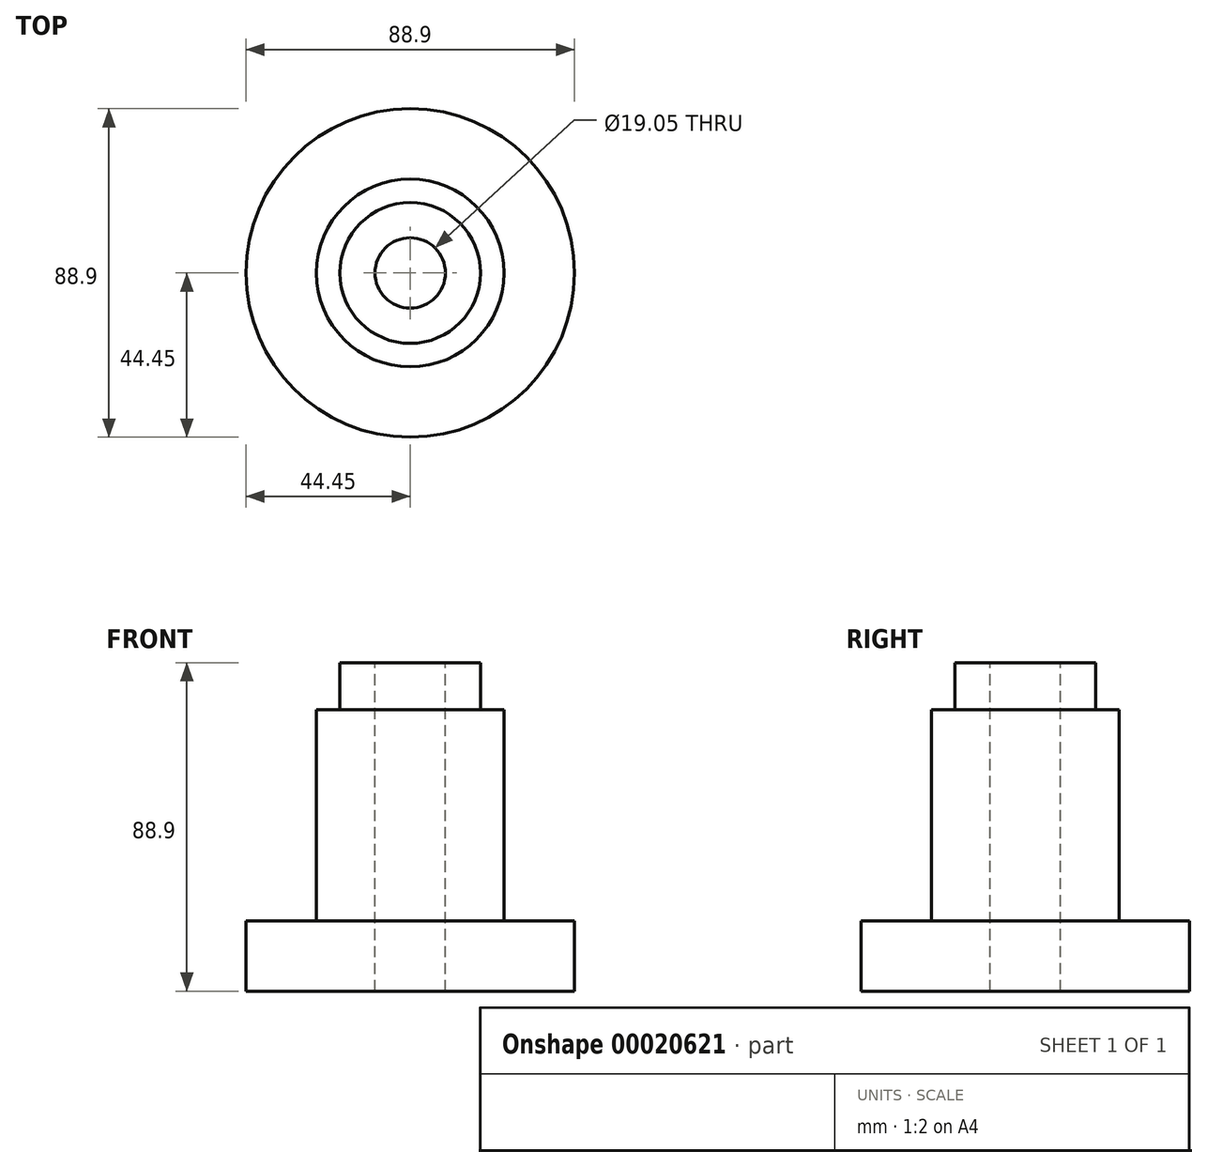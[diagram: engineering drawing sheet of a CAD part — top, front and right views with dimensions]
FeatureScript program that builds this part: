
annotation { "Feature Type Name" : "Feature", "Feature Type Description" : "" }
export const myFeature = defineFeature(function(context is Context, id is Id, definition is map)
    precondition{}
    {
        {
            var Q0;
            Q0=qCreatedBy(makeId("Front.planeOp"),FACE);
            var sketch = newSketch(context, id + "F0", { "sketchPlane" : qUnion([Q0])});
            skLineSegment(sketch, "E0", {"start": v(0, 0) * mm, "end": v(0, 88.9) * mm});
            skLineSegment(sketch, "E1", {"start": v(9.53, 51.85) * mm, "end": v(9.53, 88.9) * mm});
            skLineSegment(sketch, "E2", {"start": v(9.53, 51.85) * mm, "end": v(9.53, 0) * mm});
            skLineSegment(sketch, "E3", {"start": v(0, 0) * mm, "end": v(9.53, 0) * mm});
            skLineSegment(sketch, "E4", {"start": v(0, 88.9) * mm, "end": v(9.53, 88.9) * mm});
            skLineSegment(sketch, "E5", {"start": v(0, 0) * mm, "end": v(19.05, 0) * mm});
            skLineSegment(sketch, "E6", {"start": v(19.05, 0) * mm, "end": v(19.05, 88.9) * mm});
            skLineSegment(sketch, "E7", {"start": v(9.53, 88.9) * mm, "end": v(19.05, 88.9) * mm});
            skLineSegment(sketch, "E8", {"start": v(25.4, 76.2) * mm, "end": v(19.05, 76.2) * mm});
            skLineSegment(sketch, "E9", {"start": v(25.4, 44.45) * mm, "end": v(25.4, 76.2) * mm});
            skLineSegment(sketch, "E10", {"start": v(25.4, 76.2) * mm, "end": v(25.4, 0) * mm});
            skLineSegment(sketch, "E11", {"start": v(19.05, 0) * mm, "end": v(25.4, 0) * mm});
            skPoint(sketch, "E12.start.orphan", {"position": v(41.1, 88.9) * mm});
            skPoint(sketch, "E13.end.orphan", {"position": v(63.15, 88.9) * mm});
            skPoint(sketch, "E14.start.orphan", {"position": v(0, 44.45) * mm});
            skLineSegment(sketch, "E15", {"start": v(0, 0) * mm, "end": v(44.45, 0) * mm});
            skLineSegment(sketch, "E16", {"start": v(44.45, 0) * mm, "end": v(44.45, 19.05) * mm});
            skLineSegment(sketch, "E17", {"start": v(44.45, 19.05) * mm, "end": v(25.4, 19.05) * mm});
            skSolve(sketch);
        }
        {
            var Q0;
            {var subQ2=sQuery(id+"F0.wireOp",EDGE,"E0");Q0=makeQuery(id+"F0.imprint","IMPRINT",FACE,{"disambiguationData":[TD([[makeQuery(id+"F0.imprint","IMPRINT",EDGE,{"derivedFrom":subQ2}),-1.0]])]});}
            var Q1;
            Q1=makeQuery(id+"F0.imprint","IMPRINT",FACE,{"disambiguationData":[TD([[makeQuery(id+"F0.imprint","IMPRINT",EDGE,{"derivedFrom":sQuery(id+"F0.wireOp",EDGE,"E1")}),-1.0]])]});
            var Q2;
            {var subQ6=sQuery(id+"F0.wireOp",EDGE,"E8");Q2=makeQuery(id+"F0.imprint","IMPRINT",FACE,{"disambiguationData":[TD([[makeQuery(id+"F0.imprint","IMPRINT",EDGE,{"derivedFrom":subQ6}),1.0]])]});}
            var Q3;
            {var subQ1=sQuery(id+"F0.wireOp",EDGE,"E16");Q3=makeQuery(id+"F0.imprint","IMPRINT",FACE,{"disambiguationData":[TD([[makeQuery(id+"F0.imprint","IMPRINT",EDGE,{"derivedFrom":subQ1}),1.0]])]});}
            var Q4;
            Q4=sQuery(id+"F0.wireOp",EDGE,"E0");
            revolve(context, id + "F1", {"entities" : qUnion([Q0, Q1, Q2, Q3]), "axis" : qUnion([Q4]), "revolveType" : RevolveType.FULL});
        }
        {
            var Q0;
            Q0=makeQuery(id+"F1.opRevolve","SWEPT_FACE",FACE,{"disambiguationData":[OSD([sQuery(id+"F0.wireOp",EDGE,"E4"),sQuery(id+"F0.wireOp",EDGE,"E7")])]});
            var sketch = newSketch(context, id + "F2", { "sketchPlane" : qUnion([Q0])});
            skCircle(sketch, "E18", {"center": v(0, 0) * mm, "radius": 9.53 * mm});
            skSolve(sketch);
        }
        {
            var Q0;
            Q0=makeQuery(id+"F2.imprint","IMPRINT",FACE,{"disambiguationData":[TD([[makeQuery(id+"F2.imprint","IMPRINT",EDGE,{"derivedFrom":sQuery(id+"F2.wireOp",EDGE,"E18")}),1.0]])]});
            extrude(context, id + "F3", {"entities" : qUnion([Q0]), "operationType" : NewBodyOperationType.REMOVE, "endBound" : BoundingType.THROUGH_ALL, "oppositeDirection" : true, "depth" : 25.4 * mm});
        }
    });
